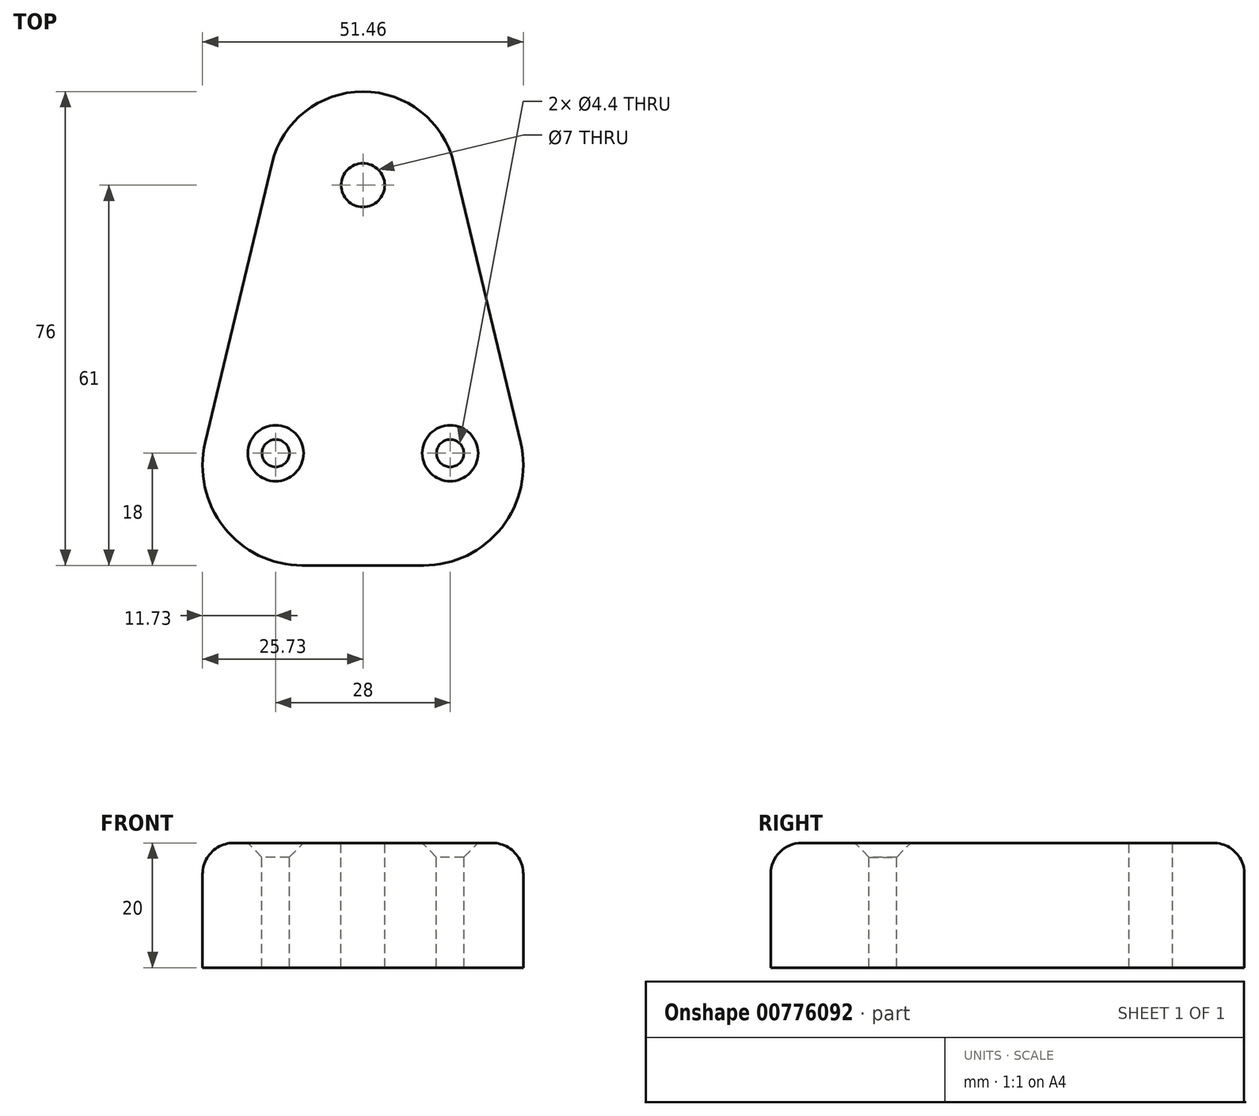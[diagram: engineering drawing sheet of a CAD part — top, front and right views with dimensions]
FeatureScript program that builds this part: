
annotation { "Feature Type Name" : "Feature", "Feature Type Description" : "" }
export const myFeature = defineFeature(function(context is Context, id is Id, definition is map)
    precondition{}
    {
        {
            var Q0;
            Q0=qCreatedBy(makeId("Top.planeOp"),FACE);
            var sketch = newSketch(context, id + "F0", { "sketchPlane" : qUnion([Q0])});
            skLineSegment(sketch, "E0.top", {"start": v(9.73, -61) * mm, "end": v(-9.73, -61) * mm});
            skLineSegment(sketch, "E0.left", {"start": v(14.59, 3.49) * mm, "end": v(25.29, -41.28) * mm});
            skLineSegment(sketch, "E0.right", {"start": v(-14.59, 3.49) * mm, "end": v(-25.29, -41.28) * mm});
            skPoint(sketch, "E0.middle", {"position": v(0, 0) * mm});
            skLineSegment(sketch, "E1", {"start": v(-14, -43) * mm, "end": v(14, -43) * mm, "construction": true});
            skPoint(sketch, "E2.visualSharp", {"position": v(-30, -61) * mm});
            skArc(sketch, "E2.filletArc", {"start": v(-25.29, -41.28) * mm, "mid": v(-22.29, -54.91) * mm, "end": v(-9.73, -61) * mm});
            skPoint(sketch, "E3.visualSharp", {"position": v(30, -61) * mm});
            skArc(sketch, "E3.filletArc", {"start": v(9.73, -61) * mm, "mid": v(22.29, -54.91) * mm, "end": v(25.29, -41.28) * mm});
            skArc(sketch, "E4", {"start": v(-14.59, 3.49) * mm, "mid": v(0, 15) * mm, "end": v(14.59, 3.49) * mm});
            skSolve(sketch);
        }
        {
            var Q0;
            Q0=makeQuery(id+"F0.imprint","IMPRINT",FACE,{"disambiguationData":[TD([[makeQuery(id+"F0.imprint","IMPRINT",EDGE,{"derivedFrom":sQuery(id+"F0.wireOp",EDGE,"E0.top")}),-1.0]])]});
            extrude(context, id + "F1", {"entities" : qUnion([Q0]), "oppositeDirection" : true, "depth" : 20 * mm, "offsetDistance" : 25 * mm});
        }
        {
            var Q0;
            Q0=sQuery(id+"F0.wireOp",VERTEX,"E1.start");
            var Q1;
            Q1=sQuery(id+"F0.wireOp",VERTEX,"E1.end");
            var Q2;
            Q2=makeQuery(id+"F1.opExtrude","SWEPT_BODY",BODY,{"disambiguationData":[OSD([sQuery(id+"F0.wireOp",EDGE,"E0.top"),sQuery(id+"F0.wireOp",EDGE,"E0.left"),sQuery(id+"F0.wireOp",EDGE,"E0.right"),sQuery(id+"F0.wireOp",EDGE,"sWGNEKWL-Ijza-Z6uH-ZLsm-gZwADiA2amFD")])]});
            hole(context, id + "F2", {"style" : HoleStyle.C_SINK, "endStyle" : HoleEndStyle.THROUGH, "standardTappedOrClearance" : lookupTablePath({ "standard" : "ISO", "fit" : "Normal", "size" : "M4", "type" : "Clearance" }), "standardBlindInLast" : lookupTablePath({ "fit" : "Standard", "standard" : "ISO", "size" : "M4", "type" : "Clearance" }), "holeDiameter" : 4.4 * mm, "cSinkDiameter" : 8.96 * mm, "cSinkAngle" : 90 * degree, "majorDiameter" : 5 * mm, "isTappedThrough" : true, "tappedDepth" : 12 * mm, "tapClearance" : 3, "locations" : qUnion([Q0, Q1]), "scope" : qUnion([Q2])});
        }
        {
            var Q0;
            Q0=makeQuery(id+"F1.opExtrude","CAP_EDGE",EDGE,{"disambiguationData":[OSD([sQuery(id+"F0.wireOp",EDGE,"E0.top")])],"isStart":true});
            var Q1;
            Q1=makeQuery(id+"F1.opExtrude","CAP_EDGE",EDGE,{"disambiguationData":[OSD([sQuery(id+"F0.wireOp",EDGE,"E0.right")])],"isStart":true});
            var Q2;
            Q2=makeQuery(id+"F1.opExtrude","CAP_EDGE",EDGE,{"disambiguationData":[OSD([sQuery(id+"F0.wireOp",EDGE,"sWGNEKWL-Ijza-Z6uH-ZLsm-gZwADiA2amFD")])],"isStart":true});
            var Q3;
            Q3=makeQuery(id+"F1.opExtrude","CAP_EDGE",EDGE,{"disambiguationData":[OSD([sQuery(id+"F0.wireOp",EDGE,"E0.left")])],"isStart":true});
            fillet(context, id + "F3", {"entities" : qUnion([Q0, Q1, Q2, Q3]), "radius" : 5 * mm, "tangentPropagation" : true, "allowEdgeOverflow" : false});
        }
        {
            var Q0;
            Q0=sQuery(id+"F0.wireOp",VERTEX,"E0.middle");
            var Q1;
            Q1=makeQuery(id+"F1.opExtrude","SWEPT_BODY",BODY,{"disambiguationData":[OSD([sQuery(id+"F0.wireOp",EDGE,"E0.top"),sQuery(id+"F0.wireOp",EDGE,"E0.left"),sQuery(id+"F0.wireOp",EDGE,"E0.right"),sQuery(id+"F0.wireOp",EDGE,"sWGNEKWL-Ijza-Z6uH-ZLsm-gZwADiA2amFD")])]});
            hole(context, id + "F4", {"style" : HoleStyle.SIMPLE, "endStyle" : HoleEndStyle.THROUGH, "standardTappedOrClearance" : lookupTablePath({ "standard" : "ISO", "size" : "7", "type" : "Drilled" }), "standardBlindInLast" : lookupTablePath({ "standard" : "ISO", "size" : "7", "type" : "Drilled" }), "holeDiameter" : 7 * mm, "majorDiameter" : 5 * mm, "isTappedThrough" : true, "tappedDepth" : 12 * mm, "tapClearance" : 3, "locations" : qUnion([Q0]), "scope" : qUnion([Q1])});
        }
    });
